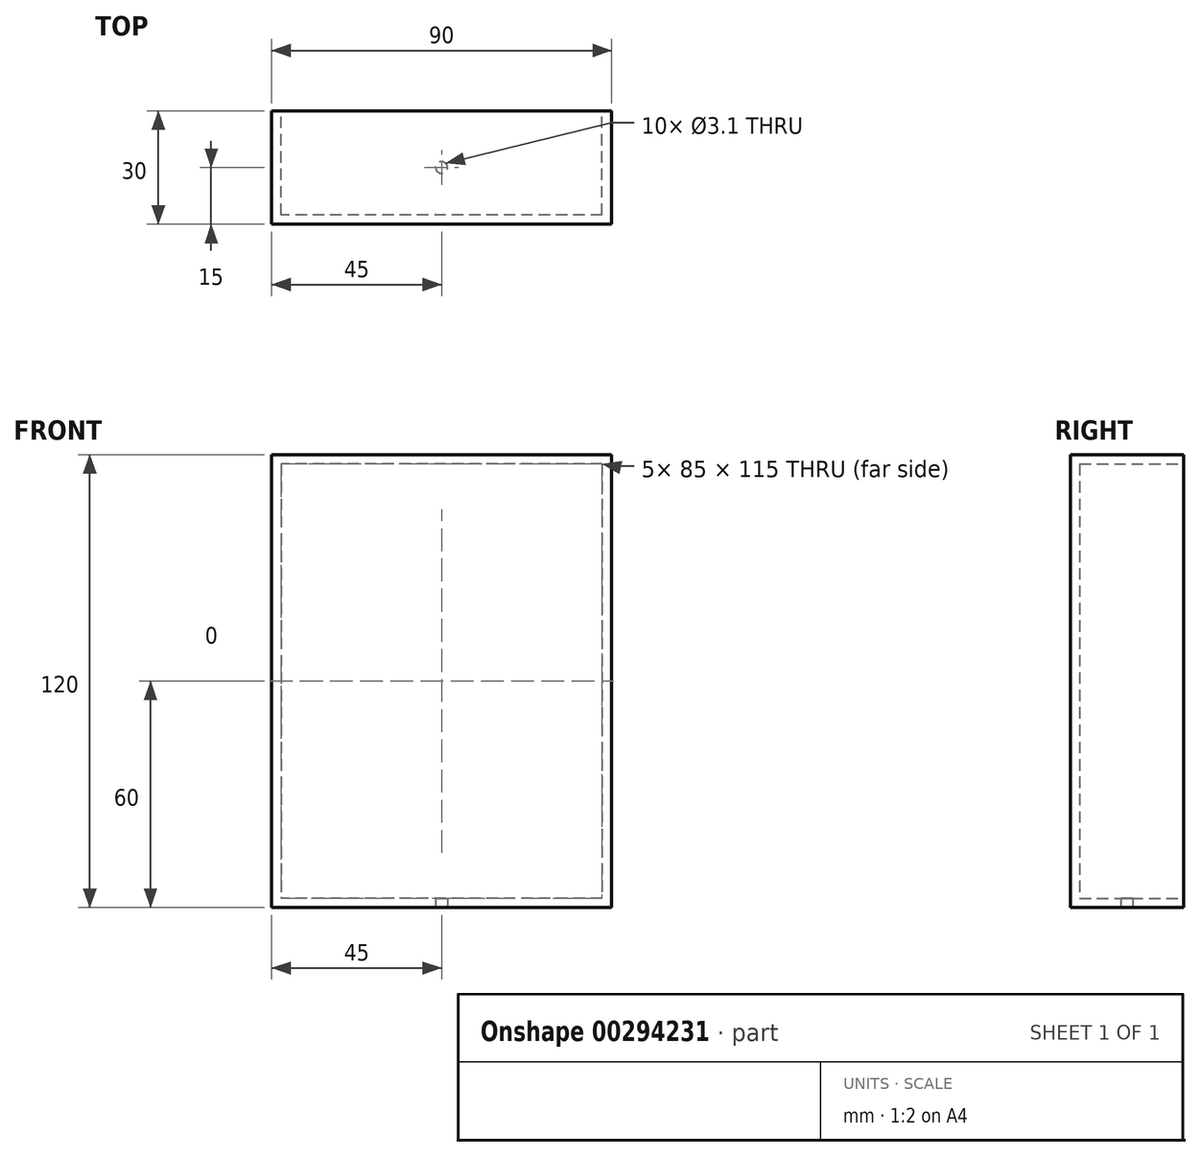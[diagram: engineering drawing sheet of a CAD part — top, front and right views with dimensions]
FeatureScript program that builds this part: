
annotation { "Feature Type Name" : "Feature", "Feature Type Description" : "" }
export const myFeature = defineFeature(function(context is Context, id is Id, definition is map)
    precondition{}
    {
        {
            var Q0;
            Q0=qCreatedBy(makeId("Front.planeOp"),FACE);
            var sketch = newSketch(context, id + "F0", { "sketchPlane" : qUnion([Q0])});
            skLineSegment(sketch, "E0.bottom", {"start": v(45, 60) * mm, "end": v(-45, 60) * mm});
            skLineSegment(sketch, "E0.top", {"start": v(45, -60) * mm, "end": v(-45, -60) * mm});
            skLineSegment(sketch, "E0.left", {"start": v(45, 60) * mm, "end": v(45, -60) * mm});
            skLineSegment(sketch, "E0.right", {"start": v(-45, 60) * mm, "end": v(-45, -60) * mm});
            skPoint(sketch, "E0.middle", {"position": v(0, 0) * mm});
            skSolve(sketch);
        }
        {
            var Q0;
            Q0 = qSketchRegion(id + "F0", true);
            extrude(context, id + "F1", {"entities" : qUnion([Q0]), "depth" : 30 * mm});
        }
        {
            var Q0;
            Q0=makeQuery(id+"F1.opExtrude","CAP_FACE",FACE,{"disambiguationData":[OSD([sQuery(id+"F0.wireOp",EDGE,"E0.bottom"),sQuery(id+"F0.wireOp",EDGE,"E0.top"),sQuery(id+"F0.wireOp",EDGE,"E0.left"),sQuery(id+"F0.wireOp",EDGE,"E0.right")])],"isStart":true});
            shell(context, id + "F2", {"entities" : qUnion([Q0]), "thickness" : 2.5 * mm});
        }
        {
            var Q0;
            Q0=makeQuery(id+"F1.opExtrude","SWEPT_FACE",FACE,{"disambiguationData":[OSD([sQuery(id+"F0.wireOp",EDGE,"E0.top")])]});
            var sketch = newSketch(context, id + "F3", { "sketchPlane" : qUnion([Q0])});
            skLineSegment(sketch, "E1", {"start": v(0, 30) * mm, "end": v(0, 0) * mm, "construction": true});
            skLineSegment(sketch, "E2", {"start": v(-45, 15) * mm, "end": v(45, 15) * mm, "construction": true});
            skCircle(sketch, "E3", {"center": v(0, 15) * mm, "radius": 1.55 * mm});
            skSolve(sketch);
        }
        {
            var Q0;
            Q0=makeQuery(id+"F3.imprint","IMPRINT",FACE,{"disambiguationData":[TD([[makeQuery(id+"F3.imprint","IMPRINT",EDGE,{"derivedFrom":sQuery(id+"F3.wireOp",EDGE,"E3")}),1.0]])]});
            extrude(context, id + "F4", {"entities" : qUnion([Q0]), "operationType" : NewBodyOperationType.REMOVE, "oppositeDirection" : true, "depth" : 25 * mm});
        }
    });
